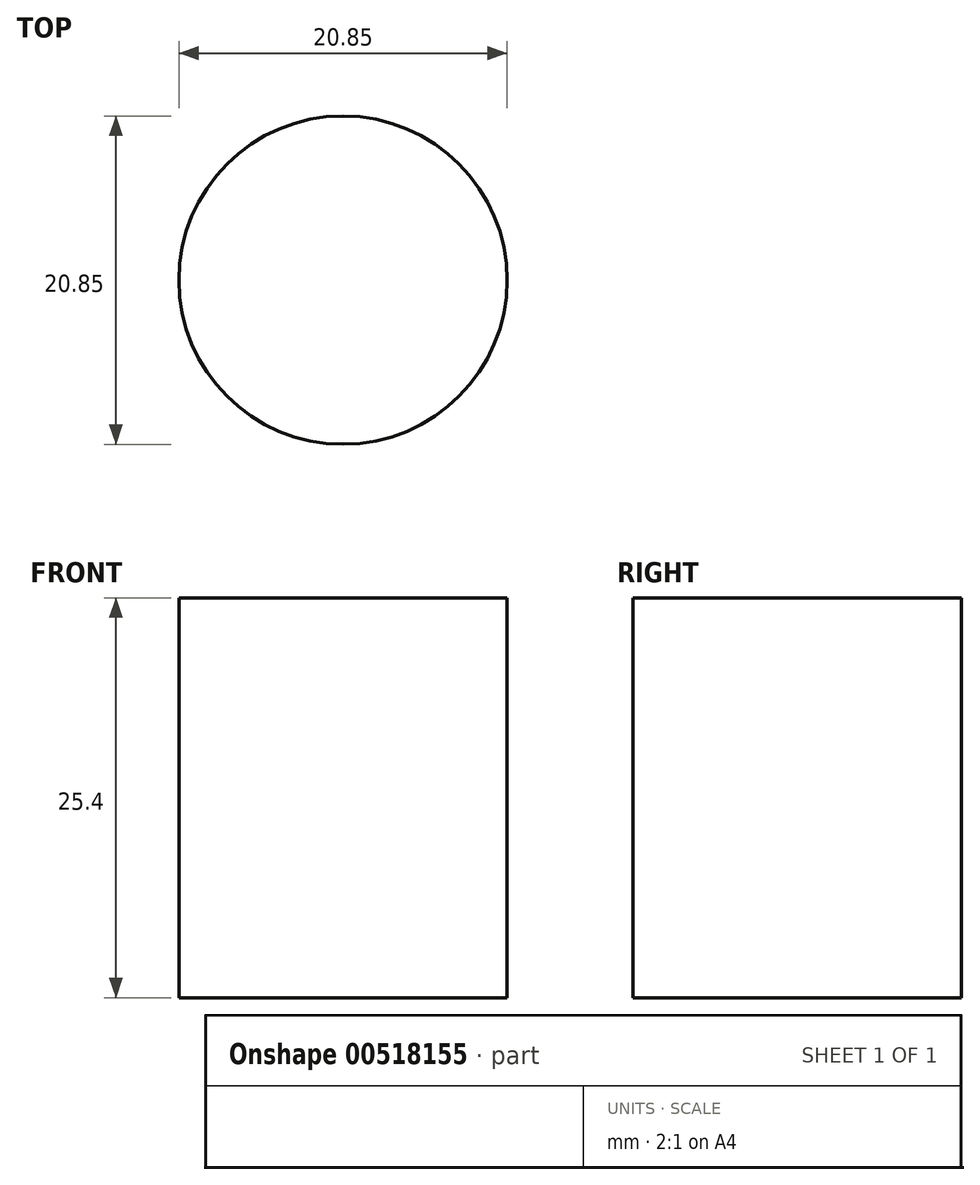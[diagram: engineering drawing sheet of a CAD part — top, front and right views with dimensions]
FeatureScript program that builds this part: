
annotation { "Feature Type Name" : "Feature", "Feature Type Description" : "" }
export const myFeature = defineFeature(function(context is Context, id is Id, definition is map)
    precondition{}
    {
        {
            var Q0;
            Q0=qCreatedBy(makeId("Top.planeOp"),FACE);
            var sketch = newSketch(context, id + "F0", { "sketchPlane" : qUnion([Q0])});
            skCircle(sketch, "E0", {"center": v(-3.02, 3.26) * mm, "radius": 10.42 * mm});
            skSolve(sketch);
        }
        {
            var Q0;
            Q0=makeQuery(id+"F0.imprint","IMPRINT",FACE,{"disambiguationData":[TD([[makeQuery(id+"F0.imprint","IMPRINT",EDGE,{"derivedFrom":sQuery(id+"F0.wireOp",EDGE,"E0")}),1.0]])]});
            extrude(context, id + "F1", {"entities" : qUnion([Q0]), "depth" : 25.4 * mm, "offsetDistance" : 25.4 * mm});
        }
    });
